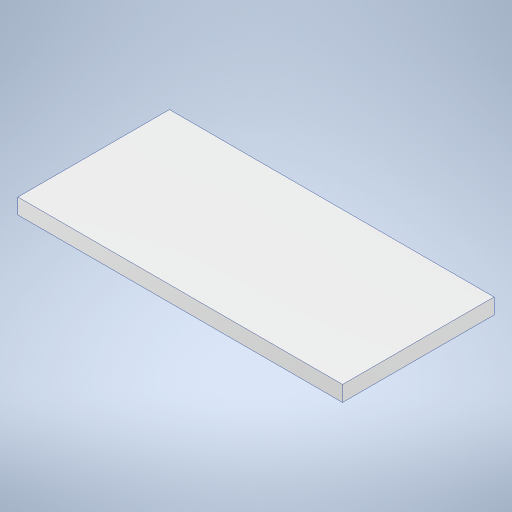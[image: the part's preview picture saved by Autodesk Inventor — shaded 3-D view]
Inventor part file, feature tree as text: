
AUTODESK INVENTOR PART (.ipt)
format: ipt  version: 2024 (Build 280153000, 153)  size: 227,840 bytes
history: native  units: mm
features: extrude x2, sketch x2
ambient origin geometry x8: Origin, YZ Plane, XZ Plane, XY Plane, X Axis, Y Axis, Z Axis, Center Point
bodies: Solid1 (feature_tree)
feature tree (4):
  extrude  "Extrusion1"  Depth=175.0mm
  extrude  "Extrusion2"  Depth=18.0mm TaperAngle=0.0deg
  sketch  "Sketch1"  dims[d0=175.0mm d1=175.0mm]
  sketch  "Sketch2"  dims[d2=12.0mm d3=0.0mm d6=18.0mm d7=0.0mm d8=100.0mm d9=100.0mm]
